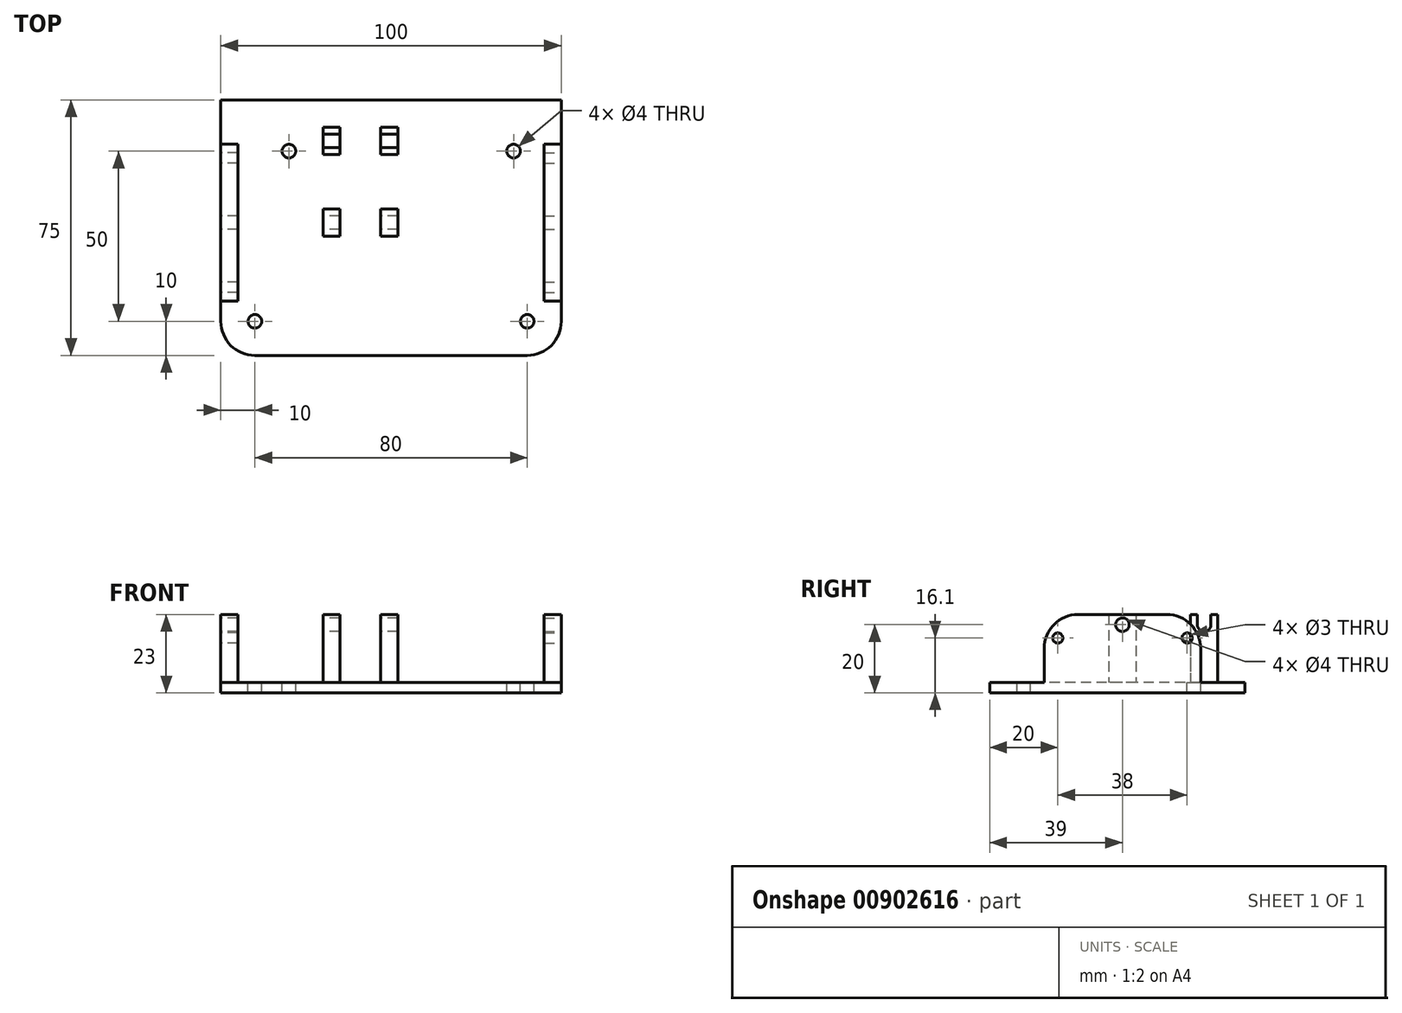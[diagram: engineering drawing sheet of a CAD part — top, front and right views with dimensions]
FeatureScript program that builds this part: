
annotation { "Feature Type Name" : "Feature", "Feature Type Description" : "" }
export const myFeature = defineFeature(function(context is Context, id is Id, definition is map)
    precondition{}
    {
        {
            var Q0;
            Q0=qCreatedBy(makeId("Top.planeOp"),FACE);
            var sketch = newSketch(context, id + "F0", { "sketchPlane" : qUnion([Q0])});
            skLineSegment(sketch, "E0.bottom", {"start": v(50, 37.5) * mm, "end": v(-50, 37.5) * mm});
            skLineSegment(sketch, "E0.top", {"start": v(40, -37.5) * mm, "end": v(-40, -37.5) * mm});
            skLineSegment(sketch, "E0.left", {"start": v(50, 37.5) * mm, "end": v(50, -27.5) * mm});
            skLineSegment(sketch, "E0.right", {"start": v(-50, 37.5) * mm, "end": v(-50, -27.5) * mm});
            skPoint(sketch, "E0.middle", {"position": v(0, 0) * mm});
            skPoint(sketch, "E1.visualSharp", {"position": v(50, -37.5) * mm});
            skArc(sketch, "E1.filletArc", {"start": v(40, -37.5) * mm, "mid": v(47.07, -34.57) * mm, "end": v(50, -27.5) * mm});
            skPoint(sketch, "E2.visualSharp", {"position": v(-50, -37.5) * mm});
            skArc(sketch, "E2.filletArc", {"start": v(-50, -27.5) * mm, "mid": v(-47.07, -34.57) * mm, "end": v(-40, -37.5) * mm});
            skSolve(sketch);
        }
        {
            var Q0;
            Q0=qSketchRegion(id+"F0",true);
            extrude(context, id + "F1", {"entities" : qUnion([Q0]), "depth" : 3 * mm, "offsetDistance" : 25.4 * mm});
        }
        {
            var Q0;
            Q0=makeQuery(id+"F1.opExtrude","SWEPT_FACE",FACE,{"disambiguationData":[OSD([sQuery(id+"F0.wireOp",EDGE,"E0.left")])]});
            var sketch = newSketch(context, id + "F2", { "sketchPlane" : qUnion([Q0])});
            skLineSegment(sketch, "E3.bottom", {"start": v(-21.5, 3) * mm, "end": v(24.5, 3) * mm});
            skLineSegment(sketch, "E3.top", {"start": v(-11.5, 23) * mm, "end": v(14.5, 23) * mm});
            skLineSegment(sketch, "E3.left", {"start": v(-21.5, 3) * mm, "end": v(-21.5, 13) * mm});
            skLineSegment(sketch, "E3.right", {"start": v(24.5, 3) * mm, "end": v(24.5, 13) * mm});
            skCircle(sketch, "E4", {"center": v(1.5, 20) * mm, "radius": 2 * mm});
            skPoint(sketch, "E4.centerSnap0", {"position": v(1.5, 23) * mm});
            skCircle(sketch, "E5", {"center": v(-17.5, 16.1) * mm, "radius": 1.5 * mm});
            skCircle(sketch, "E6", {"center": v(20.5, 16.1) * mm, "radius": 1.5 * mm});
            skPoint(sketch, "E7.visualSharp", {"position": v(-21.5, 23) * mm});
            skArc(sketch, "E7.filletArc", {"start": v(-11.5, 23) * mm, "mid": v(-18.57, 20.07) * mm, "end": v(-21.5, 13) * mm});
            skPoint(sketch, "E8.visualSharp", {"position": v(24.5, 23) * mm});
            skArc(sketch, "E8.filletArc", {"start": v(24.5, 13) * mm, "mid": v(21.57, 20.07) * mm, "end": v(14.5, 23) * mm});
            skSolve(sketch);
        }
        {
            var Q0;
            Q0=qSketchRegion(id+"F2",true);
            extrude(context, id + "F3", {"entities" : qUnion([Q0]), "operationType" : NewBodyOperationType.ADD, "oppositeDirection" : true, "depth" : 5 * mm, "offsetDistance" : 25.4 * mm});
        }
        {
            var Q0;
            Q0=makeQuery(id+"F1.opExtrude","SWEPT_FACE",FACE,{"disambiguationData":[OSD([sQuery(id+"F0.wireOp",EDGE,"E0.right")])]});
            var sketch = newSketch(context, id + "F4", { "sketchPlane" : qUnion([Q0])});
            skLineSegment(sketch, "E9.0", {"start": v(11.5, 23) * mm, "end": v(-14.5, 23) * mm});
            skArc(sketch, "E10.0", {"start": v(-24.5, 13) * mm, "mid": v(-21.57, 20.07) * mm, "end": v(-14.5, 23) * mm});
            skLineSegment(sketch, "E11.0.0", {"start": v(-24.5, 3) * mm, "end": v(21.5, 3) * mm});
            skLineSegment(sketch, "E11.0.1", {"start": v(21.5, 3) * mm, "end": v(21.5, 13) * mm});
            skArc(sketch, "E11.0.2", {"start": v(21.5, 13) * mm, "mid": v(18.57, 20.07) * mm, "end": v(11.5, 23) * mm});
            skArc(sketch, "E11.0.4", {"start": v(-14.5, 23) * mm, "mid": v(-21.57, 20.07) * mm, "end": v(-24.5, 13) * mm});
            skLineSegment(sketch, "E11.0.5", {"start": v(-24.5, 13) * mm, "end": v(-24.5, 3) * mm});
            skCircle(sketch, "E12.0", {"center": v(-20.5, 16.1) * mm, "radius": 1.5 * mm});
            skCircle(sketch, "E13.0", {"center": v(-1.5, 20) * mm, "radius": 2 * mm});
            skCircle(sketch, "E14.0", {"center": v(17.5, 16.1) * mm, "radius": 1.5 * mm});
            skSolve(sketch);
        }
        {
            var Q0;
            Q0=qSketchRegion(id+"F4",true);
            extrude(context, id + "F5", {"entities" : qUnion([Q0]), "operationType" : NewBodyOperationType.ADD, "oppositeDirection" : true, "depth" : 5 * mm, "offsetDistance" : 25.4 * mm});
        }
        {
            var Q0;
            Q0=makeQuery(id+"F1.opExtrude","CAP_FACE",FACE,{"disambiguationData":[OSD([sQuery(id+"F0.wireOp",EDGE,"E0.bottom"),sQuery(id+"F0.wireOp",EDGE,"E0.top"),sQuery(id+"F0.wireOp",EDGE,"E0.left"),sQuery(id+"F0.wireOp",EDGE,"E0.right"),sQuery(id+"F0.wireOp",EDGE,"E1.filletArc"),sQuery(id+"F0.wireOp",EDGE,"E2.filletArc")])],"isStart":false});
            var sketch = newSketch(context, id + "F6", { "sketchPlane" : qUnion([Q0])});
            skCircle(sketch, "E15", {"center": v(-30, 22.5) * mm, "radius": 2 * mm});
            skCircle(sketch, "E16", {"center": v(36, 22.5) * mm, "radius": 2 * mm});
            skCircle(sketch, "E17", {"center": v(-40, -27.5) * mm, "radius": 2 * mm});
            skCircle(sketch, "E18", {"center": v(40, -27.5) * mm, "radius": 2 * mm});
            skLineSegment(sketch, "E19.0.0", {"start": v(-50, 24.5) * mm, "end": v(-45, 24.5) * mm});
            skLineSegment(sketch, "E19.0.1", {"start": v(-45, 24.5) * mm, "end": v(-45, -21.5) * mm});
            skLineSegment(sketch, "E19.0.2", {"start": v(-45, -21.5) * mm, "end": v(-50, -21.5) * mm});
            skLineSegment(sketch, "E19.0.3", {"start": v(-50, -21.5) * mm, "end": v(-50, -27.5) * mm});
            skArc(sketch, "E19.0.4", {"start": v(-50, -27.5) * mm, "mid": v(-47.07, -34.57) * mm, "end": v(-40, -37.5) * mm});
            skLineSegment(sketch, "E19.0.5", {"start": v(-40, -37.5) * mm, "end": v(40, -37.5) * mm});
            skArc(sketch, "E19.0.6", {"start": v(40, -37.5) * mm, "mid": v(47.07, -34.57) * mm, "end": v(50, -27.5) * mm});
            skLineSegment(sketch, "E19.0.7", {"start": v(50, -27.5) * mm, "end": v(50, -21.5) * mm});
            skLineSegment(sketch, "E19.0.8", {"start": v(50, -21.5) * mm, "end": v(45, -21.5) * mm});
            skLineSegment(sketch, "E19.0.9", {"start": v(45, -21.5) * mm, "end": v(45, 24.5) * mm});
            skLineSegment(sketch, "E19.0.10", {"start": v(45, 24.5) * mm, "end": v(50, 24.5) * mm});
            skLineSegment(sketch, "E19.0.11", {"start": v(50, 24.5) * mm, "end": v(50, 37.5) * mm});
            skLineSegment(sketch, "E19.0.12", {"start": v(50, 37.5) * mm, "end": v(-50, 37.5) * mm});
            skLineSegment(sketch, "E19.0.13", {"start": v(-50, 37.5) * mm, "end": v(-50, 24.5) * mm});
            skSolve(sketch);
        }
        {
            var Q0;
            Q0=makeQuery(id+"F6.imprint","IMPRINT",FACE,{"disambiguationData":[TD([[makeQuery(id+"F6.imprint","IMPRINT",EDGE,{"derivedFrom":sQuery(id+"F6.wireOp",EDGE,"E15")}),1.0]])]});
            var Q1;
            Q1=makeQuery(id+"F6.imprint","IMPRINT",FACE,{"disambiguationData":[TD([[makeQuery(id+"F6.imprint","IMPRINT",EDGE,{"derivedFrom":sQuery(id+"F6.wireOp",EDGE,"E17")}),1.0]])]});
            var Q2;
            Q2=makeQuery(id+"F6.imprint","IMPRINT",FACE,{"disambiguationData":[TD([[makeQuery(id+"F6.imprint","IMPRINT",EDGE,{"derivedFrom":sQuery(id+"F6.wireOp",EDGE,"E18")}),1.0]])]});
            var Q3;
            Q3=makeQuery(id+"F6.imprint","IMPRINT",FACE,{"disambiguationData":[TD([[makeQuery(id+"F6.imprint","IMPRINT",EDGE,{"derivedFrom":sQuery(id+"F6.wireOp",EDGE,"E16")}),1.0]])]});
            extrude(context, id + "F7", {"entities" : qUnion([Q0, Q1, Q2, Q3]), "operationType" : NewBodyOperationType.REMOVE, "oppositeDirection" : true, "depth" : 25.4 * mm, "offsetDistance" : 25.4 * mm});
        }
        {
            var Q0;
            Q0=makeQuery(id+"F1.opExtrude","CAP_FACE",FACE,{"disambiguationData":[OSD([sQuery(id+"F0.wireOp",EDGE,"E0.bottom"),sQuery(id+"F0.wireOp",EDGE,"E0.top"),sQuery(id+"F0.wireOp",EDGE,"E0.left"),sQuery(id+"F0.wireOp",EDGE,"E0.right"),sQuery(id+"F0.wireOp",EDGE,"E1.filletArc"),sQuery(id+"F0.wireOp",EDGE,"E2.filletArc")])],"isStart":false});
            var sketch = newSketch(context, id + "F8", { "sketchPlane" : qUnion([Q0])});
            skLineSegment(sketch, "E20.bottom", {"start": v(-20, 29.5) * mm, "end": v(-15, 29.5) * mm});
            skLineSegment(sketch, "E20.top", {"start": v(-20, 21.5) * mm, "end": v(-15, 21.5) * mm});
            skLineSegment(sketch, "E20.left", {"start": v(-20, 29.5) * mm, "end": v(-20, 21.5) * mm});
            skLineSegment(sketch, "E20.right", {"start": v(-15, 29.5) * mm, "end": v(-15, 21.5) * mm});
            skLineSegment(sketch, "E21.bottom", {"start": v(-3, 29.5) * mm, "end": v(2, 29.5) * mm});
            skLineSegment(sketch, "E21.top", {"start": v(-3, 21.5) * mm, "end": v(2, 21.5) * mm});
            skLineSegment(sketch, "E21.left", {"start": v(-3, 29.5) * mm, "end": v(-3, 21.5) * mm});
            skLineSegment(sketch, "E21.right", {"start": v(2, 29.5) * mm, "end": v(2, 21.5) * mm});
            skLineSegment(sketch, "E22.bottom", {"start": v(-20, 5.5) * mm, "end": v(-15, 5.5) * mm});
            skLineSegment(sketch, "E22.top", {"start": v(-20, -2.5) * mm, "end": v(-15, -2.5) * mm});
            skLineSegment(sketch, "E22.left", {"start": v(-20, 5.5) * mm, "end": v(-20, -2.5) * mm});
            skLineSegment(sketch, "E22.right", {"start": v(-15, 5.5) * mm, "end": v(-15, -2.5) * mm});
            skLineSegment(sketch, "E23.bottom", {"start": v(-3, 5.5) * mm, "end": v(2, 5.5) * mm});
            skLineSegment(sketch, "E23.top", {"start": v(-3, -2.5) * mm, "end": v(2, -2.5) * mm});
            skLineSegment(sketch, "E23.left", {"start": v(-3, 5.5) * mm, "end": v(-3, -2.5) * mm});
            skLineSegment(sketch, "E23.right", {"start": v(2, 5.5) * mm, "end": v(2, -2.5) * mm});
            skSolve(sketch);
        }
        {
            var Q0;
            Q0=qSketchRegion(id+"F8",true);
            extrude(context, id + "F9", {"entities" : qUnion([Q0]), "operationType" : NewBodyOperationType.ADD, "depth" : 20 * mm, "offsetDistance" : 25.4 * mm});
        }
        {
            var Q0;
            Q0=makeQuery(id+"F9.opExtrude","SWEPT_FACE",FACE,{"disambiguationData":[OSD([sQuery(id+"F8.wireOp",EDGE,"E22.left")])]});
            var sketch = newSketch(context, id + "F10", { "sketchPlane" : qUnion([Q0])});
            skCircle(sketch, "E24.0", {"center": v(-1.5, 20) * mm, "radius": 2 * mm});
            skSolve(sketch);
        }
        {
            var Q0;
            Q0=qSketchRegion(id+"F10",true);
            extrude(context, id + "F11", {"entities" : qUnion([Q0]), "operationType" : NewBodyOperationType.REMOVE, "oppositeDirection" : true, "depth" : 25.4 * mm, "offsetDistance" : 25.4 * mm});
        }
        {
            var Q0;
            Q0=makeQuery(id+"F9.opExtrude","SWEPT_FACE",FACE,{"disambiguationData":[OSD([sQuery(id+"F8.wireOp",EDGE,"E20.left")])]});
            var sketch = newSketch(context, id + "F12", { "sketchPlane" : qUnion([Q0])});
            skArc(sketch, "E25", {"start": v(-27.5, 20) * mm, "mid": v(-25.5, 18) * mm, "end": v(-23.5, 20) * mm});
            skLineSegment(sketch, "E26", {"start": v(-23.5, 20) * mm, "end": v(-23.5, 23) * mm});
            skLineSegment(sketch, "E27", {"start": v(-27.5, 20) * mm, "end": v(-27.5, 23) * mm});
            skLineSegment(sketch, "E28", {"start": v(-27.5, 23) * mm, "end": v(-23.5, 23) * mm});
            skSolve(sketch);
        }
        {
            var Q0;
            Q0=qSketchRegion(id+"F12",true);
            extrude(context, id + "F13", {"entities" : qUnion([Q0]), "operationType" : NewBodyOperationType.REMOVE, "oppositeDirection" : true, "depth" : 25.4 * mm, "offsetDistance" : 25.4 * mm});
        }
    });
